# Revit family: 63_UN_LED Panel_Backlit Panel 30x120_Natec
name_source: partatom
category: Lighting Fixtures
units: mm (PartAtom-declared; Revit-internal decimal feet)

## family parameters
Always vertical = Yes
Cut with Voids When Loaded = No
Light Source = Yes
OmniClass Number = 23.80.70.11.14.11
OmniClass Title = Downlights
Part Type = Normal
Room Calculation Point = Yes
Round Connector Dimension = Use Diameter
Shared = No
Work Plane-Based = No

## types (2) — shared parameters
Apparent Load = 29 VA
Assembly Code = 63.0
Calc_L1_Symbol = 12 mm  [stored 0.0393701 ft]
Calc_L2_Symbol = 3 mm  [stored 0.00984252 ft]
Color Filter = 16777215
Dimming Lamp Color Temperature Shift = <None>
H1 = 32 mm  [stored 0.104987 ft]
Housing_Material = Laminate, White
IfcExportAs = IfcLightFixtureType
IfcExportType = USERDEFINED
L1 = 1195 mm  [stored 3.9206 ft]
L2 = 295 mm  [stored 0.967848 ft]
L3 = 20 mm  [stored 0.0656168 ft]
LED Panel = Yes
Lamp = LED
Manufacturer = Natec Lighting
Model = Backlit Panel
Tilt Angle = 90.00°
Type Comments = 30x120
URL = https://nateclighting.nl
Voltage = 230 V

## per-type parameters (varying)
| type | Luminous Flux (lm) | Photometric Web File | Wattage Comments |
| 8069-0098 30x120 4000K UGR19 | 3718 lm | 8069-0098 30x120 4000K UGR19.IES | 28.5W |
| 8069-0098 30x120 3000K UGR19 | 3740 lm | 8069-0099 30x120 3000K UGR19.IES | 28.7W |

note: [stored X ft] marks values corroborated as IEEE doubles in the binary element streams (Revit-internal decimal feet)

## geometry (parser evidence)
native form markers: Sweep x2
no freeform markers — native parametric forms only
